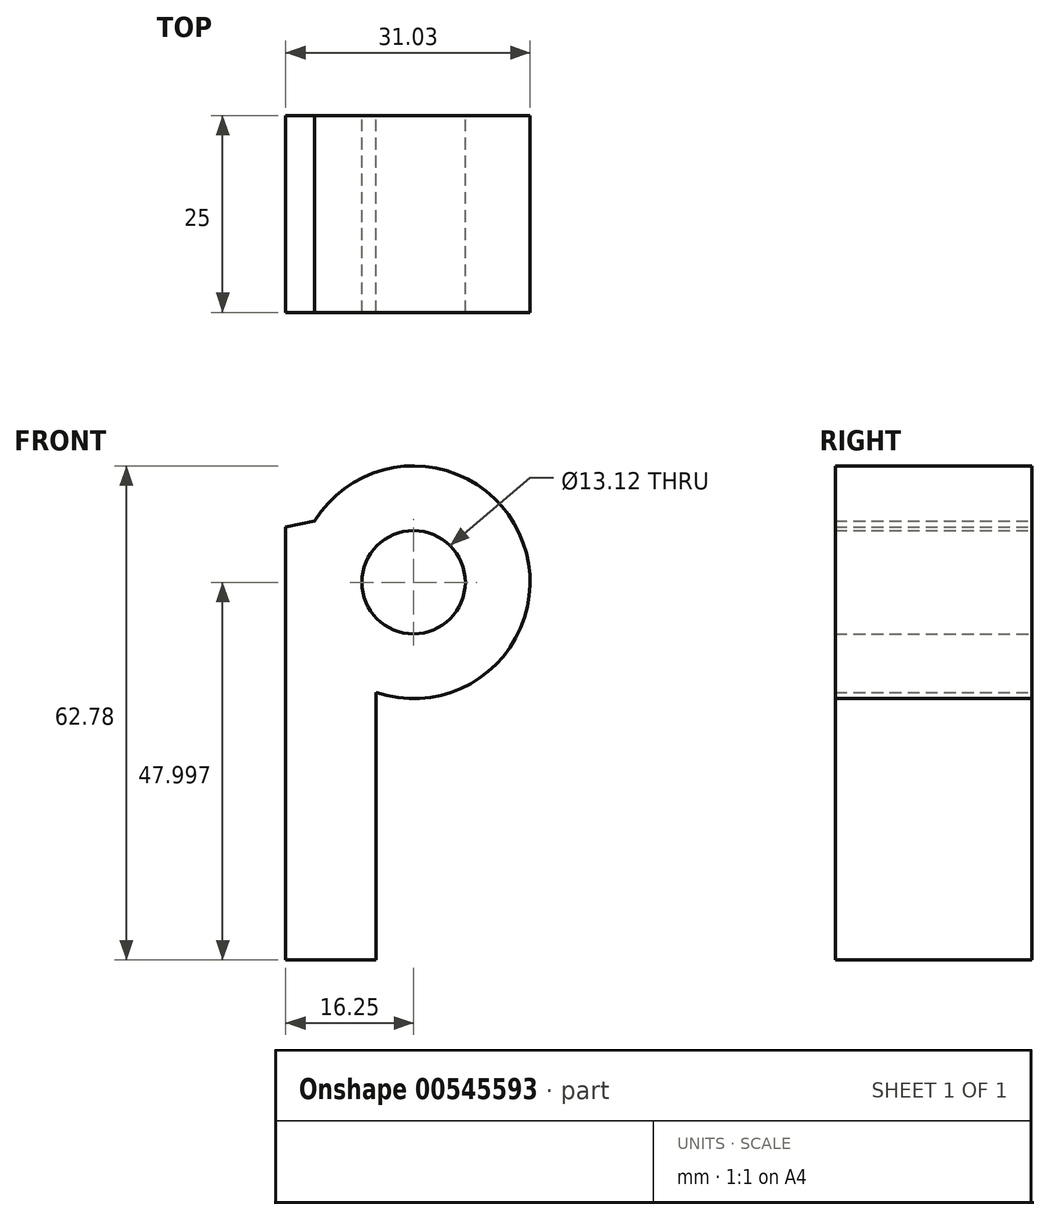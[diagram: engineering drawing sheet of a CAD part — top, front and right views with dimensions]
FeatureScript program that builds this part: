
annotation { "Feature Type Name" : "Feature", "Feature Type Description" : "" }
export const myFeature = defineFeature(function(context is Context, id is Id, definition is map)
    precondition{}
    {
        {
            var Q0;
            Q0=qCreatedBy(makeId("Front.planeOp"),FACE);
            var sketch = newSketch(context, id + "F0", { "sketchPlane" : qUnion([Q0])});
            skArc(sketch, "E0", {"start": v(0, 10) * mm, "mid": v(-20.39, -10.75) * mm, "end": v(-41.95, 8.77) * mm});
            skLineSegment(sketch, "E1", {"start": v(-41.95, 8.77) * mm, "end": v(-32, 8.77) * mm});
            skArc(sketch, "E2", {"start": v(-14, 2.25) * mm, "mid": v(-24.11, 0.08) * mm, "end": v(-31.28, 7.54) * mm});
            skArc(sketch, "E3", {"start": v(-10.25, 10.25) * mm, "mid": v(-11.13, 5.98) * mm, "end": v(-13.64, 2.41) * mm});
            skLineSegment(sketch, "E4", {"start": v(-10.25, 10.25) * mm, "end": v(-10.25, 42.25) * mm});
            skLineSegment(sketch, "E5", {"start": v(-10.25, 42.25) * mm, "end": v(0, 42.25) * mm});
            skLineSegment(sketch, "E6", {"start": v(0, 42.25) * mm, "end": v(0, 10) * mm});
            skLineSegment(sketch, "E7", {"start": v(13.25, 42.25) * mm, "end": v(13.25, -12.75) * mm});
            skLineSegment(sketch, "E8", {"start": v(13.25, -12.75) * mm, "end": v(24.75, -12.75) * mm});
            skLineSegment(sketch, "E9", {"start": v(24.75, -12.75) * mm, "end": v(24.75, 21.25) * mm});
            skArc(sketch, "E10", {"start": v(24.75, 21.25) * mm, "mid": v(43.42, 40.23) * mm, "end": v(16.95, 43.06) * mm});
            skLineSegment(sketch, "E11", {"start": v(16.95, 43.06) * mm, "end": v(13.25, 42.25) * mm});
            skCircle(sketch, "E12", {"center": v(29.5, 35.25) * mm, "radius": 6.56 * mm});
            skSolve(sketch);
        }
        {
            var Q0;
            Q0=makeQuery(id+"F0.imprint","IMPRINT",FACE,{"disambiguationData":[TD([[makeQuery(id+"F0.imprint","IMPRINT",EDGE,{"derivedFrom":sQuery(id+"F0.wireOp",EDGE,"E7")}),1.0]])]});
            extrude(context, id + "F1", {"entities" : qUnion([Q0]), "depth" : 25 * mm, "offsetDistance" : 25 * mm});
        }
    });
